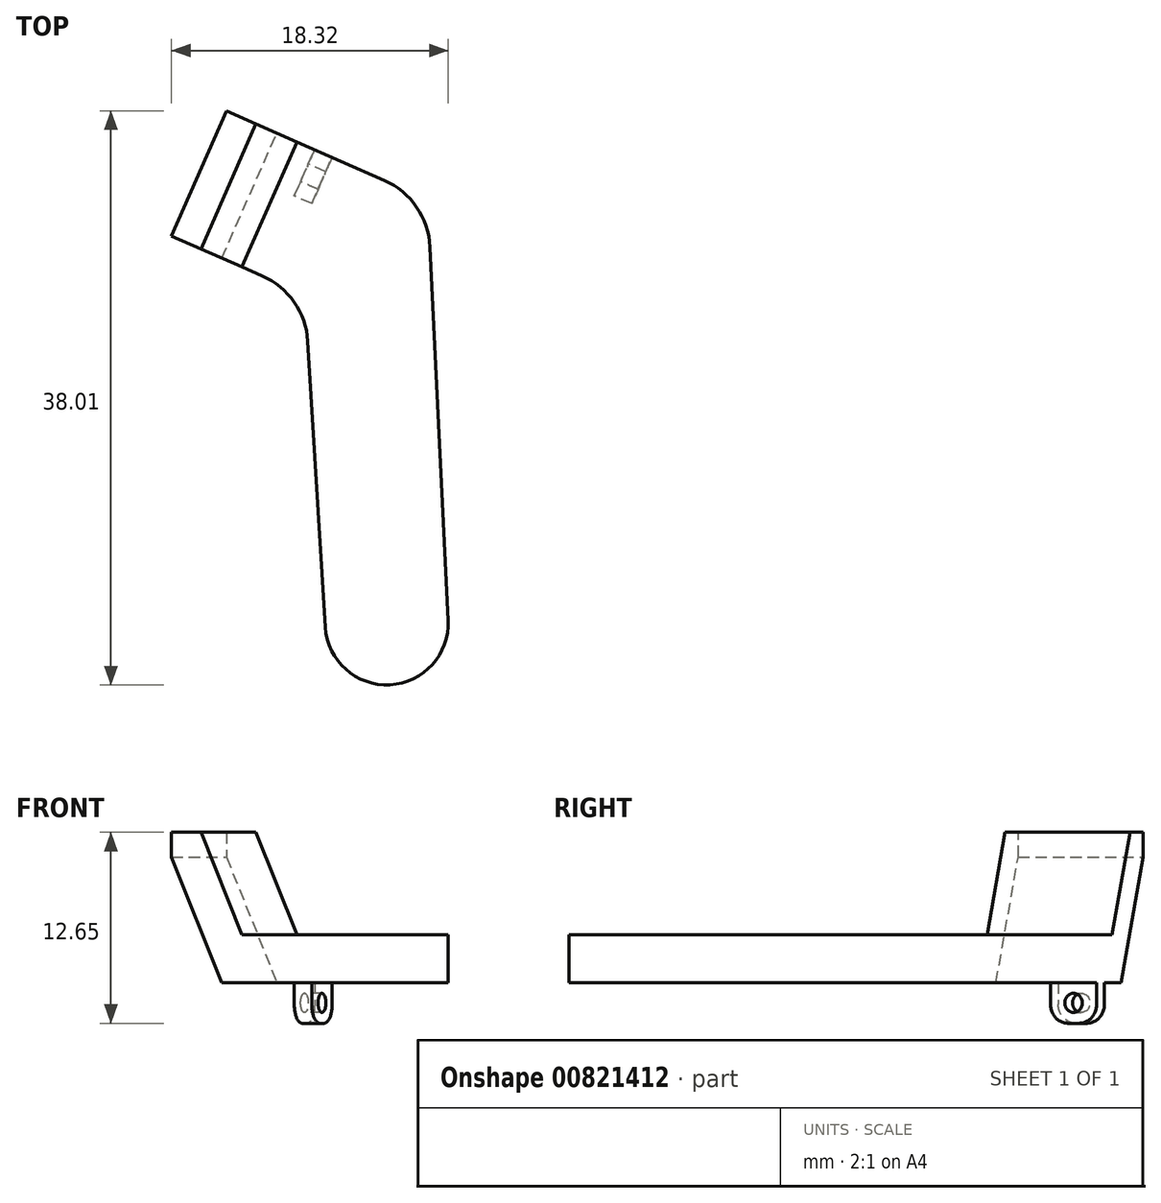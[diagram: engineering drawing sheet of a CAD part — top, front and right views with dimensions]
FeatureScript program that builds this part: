
annotation { "Feature Type Name" : "Feature", "Feature Type Description" : "" }
export const myFeature = defineFeature(function(context is Context, id is Id, definition is map)
    precondition{}
    {
        {
            var Q0;
            Q0=qCreatedBy(makeId("Top.planeOp"),FACE);
            var sketch = newSketch(context, id + "F0", { "sketchPlane" : qUnion([Q0])});
            skLineSegment(sketch, "E0", {"start": v(0, 0) * mm, "end": v(-2.56, 25.62) * mm, "construction": true});
            skLineSegment(sketch, "E1", {"start": v(-7.94, 27.96) * mm, "end": v(-2.56, 25.62) * mm, "construction": true});
            skLineSegment(sketch, "E2", {"start": v(-9.6, 23.5) * mm, "end": v(-5.96, 31.77) * mm});
            skLineSegment(sketch, "E3", {"start": v(-5.96, 31.77) * mm, "end": v(2.7, 27.96) * mm});
            skLineSegment(sketch, "E4", {"start": v(-9.6, 23.5) * mm, "end": v(-5.43, 21.66) * mm});
            skArc(sketch, "E5", {"start": v(-4.09, -0.35) * mm, "mid": v(0.2, -4.17) * mm, "end": v(4.04, 0.1) * mm});
            skPoint(sketch, "E5.third.point", {"position": v(0, -4.18) * mm});
            skLineSegment(sketch, "E6", {"start": v(-5.43, 21.66) * mm, "end": v(-4.09, -0.35) * mm});
            skLineSegment(sketch, "E7", {"start": v(2.7, 27.96) * mm, "end": v(4.04, 0.1) * mm});
            skPoint(sketch, "E8.end.orphan", {"position": v(4.04, 0) * mm});
            skSolve(sketch);
        }
        {
            var Q0;
            Q0=makeQuery(id+"F0.imprint","IMPRINT",FACE,{"disambiguationData":[TD([[makeQuery(id+"F0.imprint","IMPRINT",EDGE,{"derivedFrom":sQuery(id+"F0.wireOp",EDGE,"E2")}),-1.0]])]});
            extrude(context, id + "F1", {"entities" : qUnion([Q0]), "depth" : 3.17 * mm, "offsetDistance" : 25.4 * mm});
        }
        {
            var Q0;
            Q0=makeQuery(id+"F1.opExtrude","SWEPT_EDGE",EDGE,{"disambiguationData":[OSD([sQuery(id+"F0.wireOp",EDGE,"E3"),sQuery(id+"F0.wireOp",EDGE,"E7")])]});
            fillet(context, id + "F2", {"entities" : qUnion([Q0]), "radius" : 5.08 * mm, "tangentPropagation" : true, "allowEdgeOverflow" : false});
        }
        {
            var Q0;
            Q0=makeQuery(id+"F1.opExtrude","SWEPT_EDGE",EDGE,{"disambiguationData":[OSD([sQuery(id+"F0.wireOp",EDGE,"E4"),sQuery(id+"F0.wireOp",EDGE,"E6")])]});
            fillet(context, id + "F3", {"entities" : qUnion([Q0]), "radius" : 5.08 * mm, "tangentPropagation" : true, "allowEdgeOverflow" : false});
        }
        {
            var Q0;
            Q0=makeQuery(id+"F1.opExtrude","SWEPT_FACE",FACE,{"disambiguationData":[OSD([sQuery(id+"F0.wireOp",EDGE,"E2")])]});
            cPlane(context, id + "F4", {"entities" : qUnion([Q0]), "cplaneType" : CPlaneType.OFFSET, "offset" : 1.27 * mm, "oppositeDirection" : true, "width" : 152.4 * mm, "height" : 152.4 * mm});
        }
        {
            var Q0;
            Q0=qCreatedBy(id+"F4.planeOp",FACE);
            var sketch = newSketch(context, id + "F5", { "sketchPlane" : qUnion([Q0])});
            skLineSegment(sketch, "E9.bottom", {"start": v(-23.34, 0) * mm, "end": v(-26.68, 0) * mm});
            skLineSegment(sketch, "E9.top", {"start": v(-23.34, -2.7) * mm, "end": v(-26.68, -2.7) * mm});
            skLineSegment(sketch, "E9.left", {"start": v(-23.34, 0) * mm, "end": v(-23.34, -2.7) * mm});
            skLineSegment(sketch, "E9.right", {"start": v(-26.68, 0) * mm, "end": v(-26.68, -2.7) * mm});
            skLineSegment(sketch, "E10", {"start": v(-25, -2.7) * mm, "end": v(-25, 0) * mm, "construction": true});
            skLineSegment(sketch, "E11", {"start": v(-23.34, -1.35) * mm, "end": v(-26.68, -1.35) * mm, "construction": true});
            skPoint(sketch, "E12", {"position": v(-25, -1.35) * mm});
            skSolve(sketch);
        }
        {
            var Q0;
            Q0=makeQuery(id+"F5.imprint","IMPRINT",FACE,{"disambiguationData":[TD([[makeQuery(id+"F5.imprint","IMPRINT",EDGE,{"derivedFrom":sQuery(id+"F5.wireOp",EDGE,"E9.bottom")}),1.0]])]});
            extrude(context, id + "F6", {"entities" : qUnion([Q0]), "operationType" : NewBodyOperationType.ADD, "oppositeDirection" : true, "depth" : 1.27 * mm, "offsetDistance" : 25.4 * mm});
        }
        {
            var Q0;
            Q0=makeQuery(id+"F6.opExtrude","SWEPT_EDGE",EDGE,{"disambiguationData":[OSD([sQuery(id+"F5.wireOp",EDGE,"E9.top"),sQuery(id+"F5.wireOp",EDGE,"E9.right")])]});
            var Q1;
            Q1=makeQuery(id+"F6.opExtrude","SWEPT_EDGE",EDGE,{"disambiguationData":[OSD([sQuery(id+"F5.wireOp",EDGE,"E9.top"),sQuery(id+"F5.wireOp",EDGE,"E9.left")])]});
            fillet(context, id + "F7", {"entities" : qUnion([Q0, Q1]), "radius" : 1.27 * mm, "tangentPropagation" : true, "allowEdgeOverflow" : false});
        }
        {
            var Q0;
            Q0=sQuery(id+"F5.wireOp",VERTEX,"E12");
            var Q1;
            Q1=makeQuery(id+"F1.opExtrude","SWEPT_BODY",BODY,{"disambiguationData":[OSD([sQuery(id+"F0.wireOp",EDGE,"E2"),sQuery(id+"F0.wireOp",EDGE,"E3"),sQuery(id+"F0.wireOp",EDGE,"E4"),sQuery(id+"F0.wireOp",EDGE,"E5"),sQuery(id+"F0.wireOp",EDGE,"E6"),sQuery(id+"F0.wireOp",EDGE,"E7")])]});
            hole(context, id + "F8", {"style" : HoleStyle.SIMPLE, "endStyle" : HoleEndStyle.THROUGH, "holeDiameter" : 1.27 * mm, "majorDiameter" : 6.35 * mm, "isTappedThrough" : true, "tappedDepth" : 12.7 * mm, "tapClearance" : 3, "locations" : qUnion([Q0]), "scope" : qUnion([Q1])});
        }
        {
            var Q0;
            Q0=makeQuery(id+"F1.opExtrude","SWEPT_FACE",FACE,{"disambiguationData":[OSD([sQuery(id+"F0.wireOp",EDGE,"E3")])]});
            var sketch = newSketch(context, id + "F9", { "sketchPlane" : qUnion([Q0])});
            skLineSegment(sketch, "E13.0", {"start": v(18.25, 3.18) * mm, "end": v(18.25, 0) * mm});
            skLineSegment(sketch, "E14", {"start": v(18.25, 3.18) * mm, "end": v(21.22, 9.95) * mm});
            skLineSegment(sketch, "E15", {"start": v(21.22, 9.95) * mm, "end": v(23.35, 9.95) * mm});
            skLineSegment(sketch, "E16", {"start": v(23.35, 8.3) * mm, "end": v(19.7, 0) * mm});
            skLineSegment(sketch, "E17", {"start": v(19.7, 0) * mm, "end": v(18.25, 0) * mm});
            skLineSegment(sketch, "E18", {"start": v(23.35, 9.95) * mm, "end": v(23.35, 8.3) * mm});
            skSolve(sketch);
        }
        {
            var Q0;
            Q0=makeQuery(id+"F9.imprint","IMPRINT",FACE,{"disambiguationData":[TD([[makeQuery(id+"F9.imprint","IMPRINT",EDGE,{"derivedFrom":sQuery(id+"F9.wireOp",EDGE,"E13.0")}),1.0]])]});
            var Q1;
            Q1=makeQuery(id+"F1.opExtrude","SWEPT_FACE",FACE,{"disambiguationData":[OSD([sQuery(id+"F0.wireOp",EDGE,"E4")])]});
            extrude(context, id + "F10", {"entities" : qUnion([Q0]), "operationType" : NewBodyOperationType.ADD, "endBound" : BoundingType.UP_TO_SURFACE, "oppositeDirection" : true, "depth" : 25.4 * mm, "endBoundEntityFace" : qUnion([Q1]), "offsetDistance" : 25.4 * mm});
        }
    });
